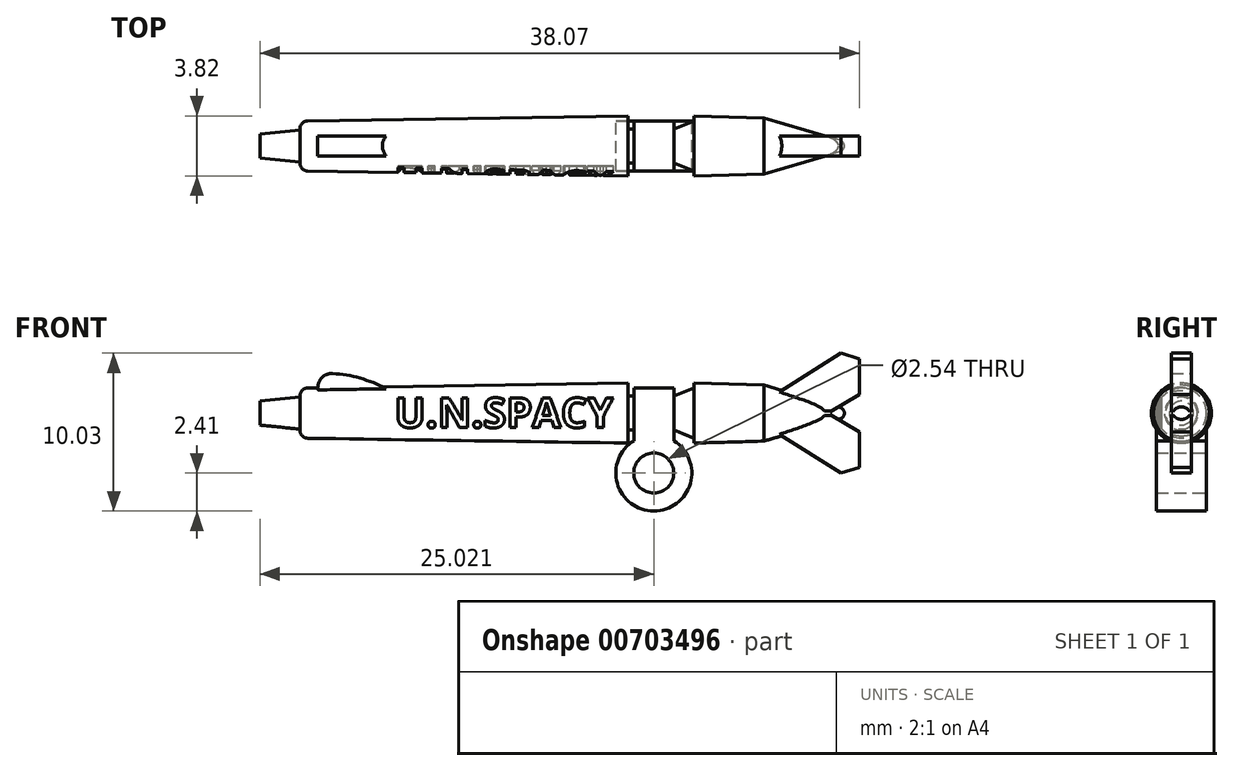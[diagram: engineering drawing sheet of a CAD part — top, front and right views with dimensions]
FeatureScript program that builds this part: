
annotation { "Feature Type Name" : "Feature", "Feature Type Description" : "" }
export const myFeature = defineFeature(function(context is Context, id is Id, definition is map)
    precondition{}
    {
        {
            var Q0;
            Q0=qCreatedBy(makeId("Front.planeOp"),FACE);
            var sketch = newSketch(context, id + "F0", { "sketchPlane" : qUnion([Q0])});
            skLineSegment(sketch, "E0", {"start": v(-36.83, 0) * mm, "end": v(32.69, 0) * mm, "construction": true});
            skLineSegment(sketch, "E1", {"start": v(-23.37, 0) * mm, "end": v(-23.37, 0.76) * mm});
            skLineSegment(sketch, "E2", {"start": v(-23.37, 0.76) * mm, "end": v(-20.83, 1.02) * mm});
            skLineSegment(sketch, "E3", {"start": v(-20.83, 1.02) * mm, "end": v(-20.83, 1.59) * mm});
            skLineSegment(sketch, "E4", {"start": v(-20.83, 1.59) * mm, "end": v(0, 1.9) * mm});
            skLineSegment(sketch, "E5", {"start": v(0, 1.9) * mm, "end": v(0, 1.08) * mm});
            skLineSegment(sketch, "E6", {"start": v(0, 1.08) * mm, "end": v(0.38, 1.08) * mm});
            skLineSegment(sketch, "E7", {"start": v(0.38, 1.08) * mm, "end": v(0.38, 1.59) * mm});
            skLineSegment(sketch, "E8", {"start": v(0.38, 1.59) * mm, "end": v(2.92, 1.59) * mm});
            skLineSegment(sketch, "E9", {"start": v(2.92, 1.59) * mm, "end": v(2.92, 1.08) * mm});
            skLineSegment(sketch, "E10", {"start": v(2.92, 1.08) * mm, "end": v(4.2, 1.59) * mm});
            skLineSegment(sketch, "E11", {"start": v(4.2, 1.59) * mm, "end": v(4.2, 1.9) * mm});
            skLineSegment(sketch, "E12", {"start": v(4.2, 1.9) * mm, "end": v(8.64, 1.78) * mm});
            skLineSegment(sketch, "E13", {"start": v(8.64, 1.78) * mm, "end": v(13.48, 0.37) * mm});
            skLineSegment(sketch, "E14", {"start": v(13.75, 0) * mm, "end": v(-23.37, 0) * mm});
            skArc(sketch, "E15", {"start": v(13.75, 0) * mm, "mid": v(13.68, 0.23) * mm, "end": v(13.48, 0.37) * mm});
            skSolve(sketch);
        }
        {
            var Q0;
            Q0=qSketchRegion(id+"F0",true);
            var Q1;
            Q1=sQuery(id+"F0.wireOp",EDGE,"E14");
            revolve(context, id + "F1", {"entities" : qUnion([Q0]), "axis" : qUnion([Q1]), "revolveType" : RevolveType.FULL});
        }
        {
            var Q0;
            Q0=makeQuery(id+"F1.opRevolve","SWEPT_EDGE",EDGE,{"disambiguationData":[OSD([sQuery(id+"F0.wireOp",EDGE,"E3"),sQuery(id+"F0.wireOp",EDGE,"E4")])]});
            fillet(context, id + "F2", {"entities" : qUnion([Q0]), "radius" : 0.5 * mm, "allowEdgeOverflow" : false});
        }
        {
            var Q0;
            Q0=qCreatedBy(makeId("Front.planeOp"),FACE);
            var sketch = newSketch(context, id + "F3", { "sketchPlane" : qUnion([Q0])});
            skArc(sketch, "E16", {"start": v(-18.75, 2.51) * mm, "mid": v(-19.69, 1.7) * mm, "end": v(-18.89, 0.74) * mm});
            skArc(sketch, "E17", {"start": v(-14.17, 0.74) * mm, "mid": v(-16.32, 2) * mm, "end": v(-18.75, 2.51) * mm});
            skLineSegment(sketch, "E18", {"start": v(-18.89, 0.74) * mm, "end": v(-14.17, 0.74) * mm});
            skLineSegment(sketch, "E19", {"start": v(8.93, 0.9) * mm, "end": v(13.54, 3.81) * mm});
            skLineSegment(sketch, "E20", {"start": v(13.54, 3.81) * mm, "end": v(14.7, 3.45) * mm});
            skLineSegment(sketch, "E21", {"start": v(14.7, 3.45) * mm, "end": v(14.7, 1.2) * mm});
            skLineSegment(sketch, "E22", {"start": v(14.7, 1.2) * mm, "end": v(12.83, 0.09) * mm});
            skLineSegment(sketch, "E23", {"start": v(12.5, 0.05) * mm, "end": v(8.93, 0.9) * mm});
            skLineSegment(sketch, "E24.MirrorCS", {"start": v(14.7, -1.2) * mm, "end": v(12.83, -0.09) * mm});
            skLineSegment(sketch, "E25.MirrorCS", {"start": v(12.5, -0.05) * mm, "end": v(8.93, -0.9) * mm});
            skPoint(sketch, "E26.orphan", {"position": v(13.54, -3.81) * mm});
            skPoint(sketch, "E27.orphan", {"position": v(14.7, -3.45) * mm});
            skLineSegment(sketch, "E28.bottom", {"start": v(12.5, 0.14) * mm, "end": v(12.83, 0.14) * mm});
            skLineSegment(sketch, "E28.top", {"start": v(12.5, -0.15) * mm, "end": v(12.83, -0.15) * mm});
            skLineSegment(sketch, "E28.left", {"start": v(12.5, 0.14) * mm, "end": v(12.5, 0.05) * mm});
            skLineSegment(sketch, "E28.right", {"start": v(12.83, 0.14) * mm, "end": v(12.83, 0.09) * mm});
            skPoint(sketch, "E29.orphan", {"position": v(12.68, 0) * mm});
            skLineSegment(sketch, "E30.trimOffspring", {"start": v(12.83, -0.09) * mm, "end": v(12.83, -0.15) * mm});
            skLineSegment(sketch, "E31.trimOffspring", {"start": v(12.5, -0.05) * mm, "end": v(12.5, -0.15) * mm});
            skLineSegment(sketch, "E32.MirrorCS", {"start": v(14.7, -3.45) * mm, "end": v(14.7, -1.2) * mm});
            skLineSegment(sketch, "E33.MirrorCS", {"start": v(13.54, -3.81) * mm, "end": v(14.7, -3.45) * mm});
            skLineSegment(sketch, "E34.MirrorCS", {"start": v(8.93, -0.9) * mm, "end": v(13.54, -3.81) * mm});
            skSolve(sketch);
        }
        {
            var Q0;
            Q0=qSketchRegion(id+"F3",true);
            extrude(context, id + "F4", {"entities" : qUnion([Q0]), "operationType" : NewBodyOperationType.ADD, "endBound" : BoundingType.SYMMETRIC, "depth" : 1.27 * mm, "offsetDistance" : 25.4 * mm});
        }
        {
            var Q0;
            Q0=qCreatedBy(makeId("Front.planeOp"),FACE);
            cPlane(context, id + "F5", {"entities" : qUnion([Q0]), "cplaneType" : CPlaneType.OFFSET, "offset" : 1.27 * mm, "width" : 152.4 * mm, "height" : 152.4 * mm});
        }
        {
            var Q0;
            Q0=qCreatedBy(id+"F5.planeOp",FACE);
            var sketch = newSketch(context, id + "F6", { "sketchPlane" : qUnion([Q0])});
            skText(sketch, "E35", { "text": "U.N.SPACY", "fontName": "OpenSans-Bold.ttf"});
            const initialGuessF6  = {"E35": [-0.01483, -0.00092, 1, 0, 0.0019]};
            skSetInitialGuess(sketch, initialGuessF6);
            skSolve(sketch);
        }
        {
            var Q0;
            Q0=qSketchRegion(id+"F6",true);
            extrude(context, id + "F7", {"entities" : qUnion([Q0]), "operationType" : NewBodyOperationType.REMOVE, "depth" : 25.4 * mm, "offsetDistance" : 25.4 * mm});
        }
        {
            var Q0;
            Q0=qCreatedBy(makeId("Front.planeOp"),FACE);
            var sketch = newSketch(context, id + "F8", { "sketchPlane" : qUnion([Q0])});
            skLineSegment(sketch, "E36", {"start": v(0.38, 0) * mm, "end": v(0.38, -1.76) * mm});
            skLineSegment(sketch, "E37", {"start": v(2.92, -1.76) * mm, "end": v(2.92, 0) * mm});
            skLineSegment(sketch, "E38", {"start": v(2.92, 0) * mm, "end": v(0.38, 0) * mm});
            skPoint(sketch, "E39.centerSnap0", {"position": v(1.65, 0) * mm});
            skCircle(sketch, "E40", {"center": v(1.65, -3.81) * mm, "radius": 1.27 * mm});
            skArc(sketch, "E41", {"start": v(0.38, -1.76) * mm, "mid": v(1.65, -6.22) * mm, "end": v(2.92, -1.76) * mm});
            skSolve(sketch);
        }
        {
            var Q0;
            Q0 = qSketchRegion(id + "F8", true);
            extrude(context, id + "F9", {"entities" : qUnion([Q0]), "operationType" : NewBodyOperationType.ADD, "endBound" : BoundingType.SYMMETRIC, "depth" : 3.17 * mm, "offsetDistance" : 25.4 * mm});
        }
    });
